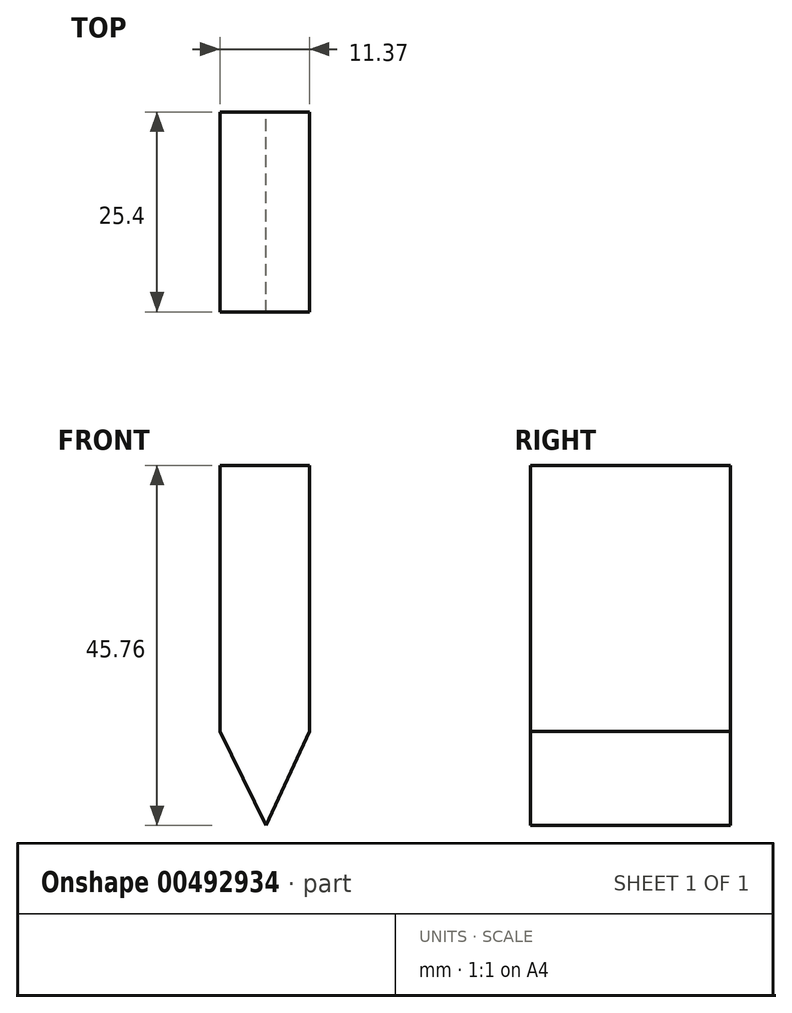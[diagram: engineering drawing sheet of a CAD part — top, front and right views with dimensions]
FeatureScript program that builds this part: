
annotation { "Feature Type Name" : "Feature", "Feature Type Description" : "" }
export const myFeature = defineFeature(function(context is Context, id is Id, definition is map)
    precondition{}
    {
        {
            var Q0;
            Q0=qCreatedBy(makeId("Front.planeOp"),FACE);
            var sketch = newSketch(context, id + "F0", { "sketchPlane" : qUnion([Q0])});
            skLineSegment(sketch, "E0", {"start": v(-27.1, 40.37) * mm, "end": v(-27.1, 6.56) * mm});
            skLineSegment(sketch, "E1", {"start": v(-27.1, 6.56) * mm, "end": v(-21.28, -5.4) * mm});
            skLineSegment(sketch, "E2", {"start": v(-21.28, -5.4) * mm, "end": v(-15.74, 6.56) * mm});
            skLineSegment(sketch, "E3", {"start": v(-15.74, 6.56) * mm, "end": v(-15.74, 40.37) * mm});
            skLineSegment(sketch, "E4", {"start": v(-15.74, 40.37) * mm, "end": v(-27.1, 40.37) * mm});
            skArc(sketch, "E5", {"start": v(-15.74, 40.37) * mm, "mid": v(-21.42, 53.3) * mm, "end": v(-27.1, 40.37) * mm});
            skSolve(sketch);
        }
        {
            var Q0;
            Q0=makeQuery(id+"F0.imprint","IMPRINT",FACE,{"disambiguationData":[TD([[makeQuery(id+"F0.imprint","IMPRINT",EDGE,{"derivedFrom":sQuery(id+"F0.wireOp",EDGE,"E0")}),1.0]])]});
            var sketch = newSketch(context, id + "F1", { "sketchPlane" : qUnion([Q0])});
            skSolve(sketch);
        }
        {
            var Q0;
            Q0=makeQuery(id+"F1.imprint","IMPRINT",FACE,{"disambiguationData":[TD([[makeQuery(id+"F1.imprint","IMPRINT",EDGE,{"derivedFrom":makeQuery(id+"F0.imprint","IMPRINT",EDGE,{"derivedFrom":sQuery(id+"F0.wireOp",EDGE,"E0")})}),1.0]])]});
            extrude(context, id + "F2", {"entities" : qUnion([Q0]), "depth" : 25.4 * mm});
        }
    });
